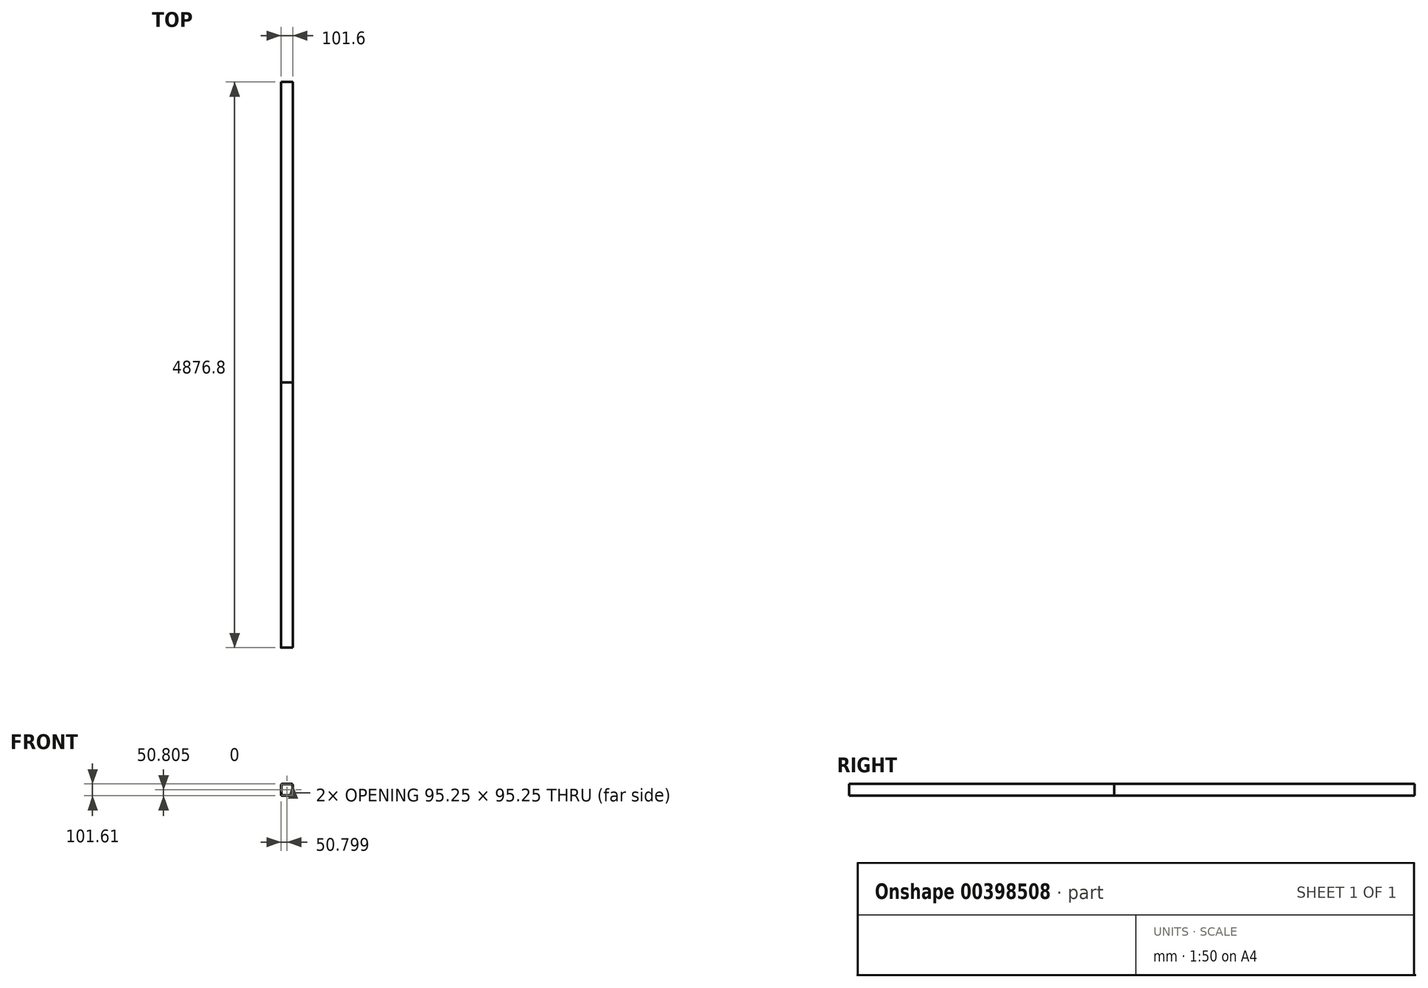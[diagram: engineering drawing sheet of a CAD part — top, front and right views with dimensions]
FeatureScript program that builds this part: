
annotation { "Feature Type Name" : "Feature", "Feature Type Description" : "" }
export const myFeature = defineFeature(function(context is Context, id is Id, definition is map)
    precondition{}
    {
        {
            var Q0;
            Q0=qCreatedBy(makeId("Front.planeOp"),FACE);
            var sketch = newSketch(context, id + "F0", { "sketchPlane" : qUnion([Q0])});
            skLineSegment(sketch, "E0.bottom", {"start": v(-9.65, 3.18) * mm, "end": v(-92.2, 3.17) * mm});
            skLineSegment(sketch, "E0.top", {"start": v(-9.65, 104.77) * mm, "end": v(-92.2, 104.77) * mm});
            skLineSegment(sketch, "E0.left", {"start": v(-0.12, 12.7) * mm, "end": v(-0.12, 95.25) * mm});
            skLineSegment(sketch, "E0.right", {"start": v(-101.72, 12.7) * mm, "end": v(-101.72, 95.25) * mm});
            skLineSegment(sketch, "E1.bottom", {"start": v(-92.2, 101.6) * mm, "end": v(-9.65, 101.6) * mm});
            skLineSegment(sketch, "E1.top", {"start": v(-92.2, 6.35) * mm, "end": v(-9.65, 6.35) * mm});
            skLineSegment(sketch, "E1.left", {"start": v(-98.55, 95.25) * mm, "end": v(-98.55, 12.7) * mm});
            skLineSegment(sketch, "E1.right", {"start": v(-3.3, 95.25) * mm, "end": v(-3.3, 12.7) * mm});
            skArc(sketch, "E2", {"start": v(-92.2, 101.6) * mm, "mid": v(-96.69, 99.74) * mm, "end": v(-98.55, 95.25) * mm});
            skArc(sketch, "E3", {"start": v(-92.2, 104.77) * mm, "mid": v(-98.93, 101.99) * mm, "end": v(-101.72, 95.25) * mm});
            skArc(sketch, "E4", {"start": v(-3.3, 95.25) * mm, "mid": v(-5.16, 99.74) * mm, "end": v(-9.65, 101.6) * mm});
            skArc(sketch, "E5", {"start": v(-0.12, 95.25) * mm, "mid": v(-2.91, 101.99) * mm, "end": v(-9.65, 104.78) * mm});
            skArc(sketch, "E6", {"start": v(-98.55, 12.7) * mm, "mid": v(-96.69, 8.2) * mm, "end": v(-92.2, 6.35) * mm});
            skArc(sketch, "E7", {"start": v(-9.65, 6.35) * mm, "mid": v(-5.16, 8.2) * mm, "end": v(-3.3, 12.7) * mm});
            skArc(sketch, "E8", {"start": v(-9.65, 3.17) * mm, "mid": v(-2.91, 5.96) * mm, "end": v(-0.12, 12.7) * mm});
            skArc(sketch, "E9", {"start": v(-101.72, 12.7) * mm, "mid": v(-98.93, 5.96) * mm, "end": v(-92.2, 3.17) * mm});
            skSolve(sketch);
        }
        {
            var Q0;
            Q0 = qSketchRegion(id + "F0", true);
            extrude(context, id + "F1", {"entities" : qUnion([Q0]), "depth" : 4876.8 * mm});
        }
        {
            var Q0;
            Q0 = qSketchRegion(id + "F0", true);
            extrude(context, id + "F2", {"entities" : qUnion([Q0]), "depth" : 2590.8 * mm});
        }
    });
